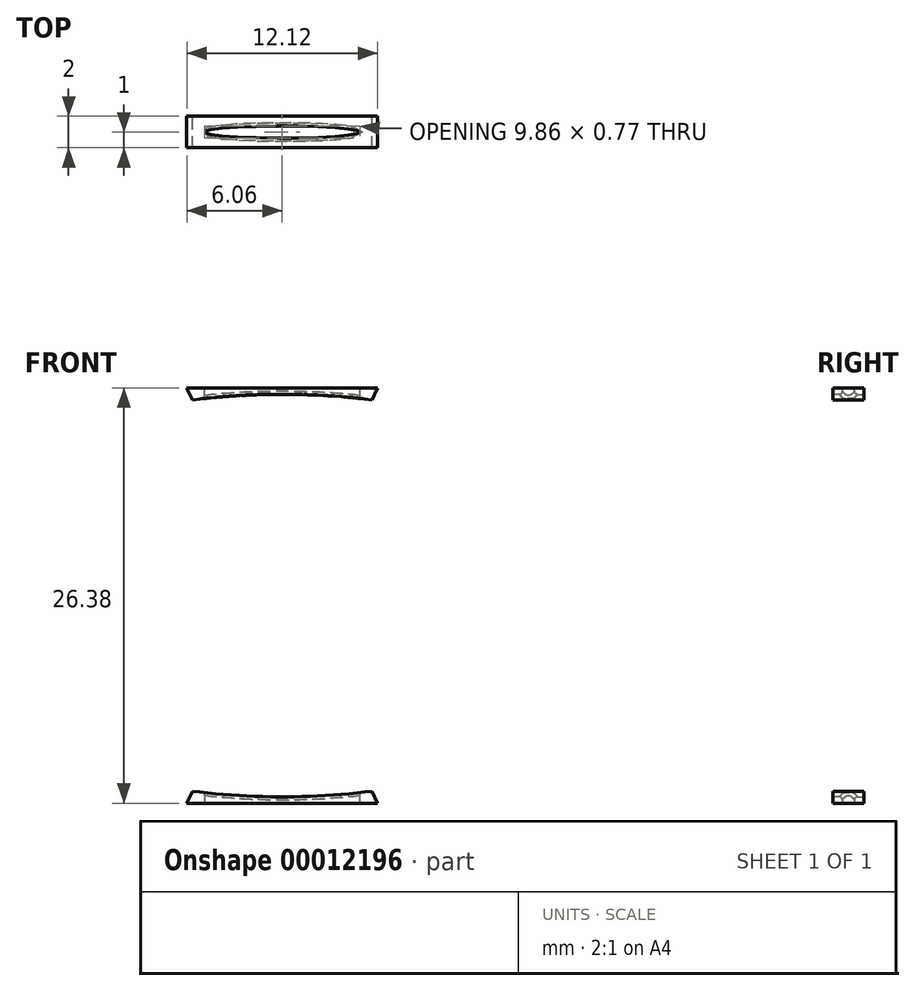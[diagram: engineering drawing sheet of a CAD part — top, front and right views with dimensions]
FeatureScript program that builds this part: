
annotation { "Feature Type Name" : "Feature", "Feature Type Description" : "" }
export const myFeature = defineFeature(function(context is Context, id is Id, definition is map)
    precondition{}
    {
        {
            var Q0;
            Q0=qCreatedBy(makeId("Front.planeOp"),FACE);
            var sketch = newSketch(context, id + "F0", { "sketchPlane" : qUnion([Q0])});
            skEllipse(sketch, "E0", {"center": v(0, 0) * mm, "majorRadius": 24.48 * mm, "minorRadius": 12.78 * mm, "majorAxis": v(1, 0)});
            skFitSpline(sketch, "E1.0", {"points": [v(25.2, -1.41) * mm, v(25.33, 0) * mm, v(25.2, 1.41) * mm, v(24.67, 3.25) * mm, v(23.65, 5) * mm, v(22.19, 6.6) * mm, v(20.44, 8.13) * mm, v(17.8, 9.8) * mm, v(14.6, 11.18) * mm, v(11.77, 12.06) * mm, v(8.8, 12.8) * mm, v(5.68, 13.29) * mm, v(2.45, 13.54) * mm, v(0, 13.6) * mm, v(-2.45, 13.54) * mm, v(-5.68, 13.29) * mm, v(-8.8, 12.8) * mm, v(-11.77, 12.06) * mm, v(-14.6, 11.18) * mm, v(-17.8, 9.8) * mm, v(-20.44, 8.13) * mm, v(-22.19, 6.6) * mm, v(-23.65, 5) * mm, v(-24.67, 3.25) * mm, v(-25.2, 1.41) * mm, v(-25.33, 0) * mm, v(-25.2, -1.41) * mm, v(-24.67, -3.25) * mm, v(-23.65, -5) * mm, v(-22.19, -6.6) * mm, v(-20.44, -8.13) * mm, v(-17.8, -9.8) * mm, v(-14.6, -11.18) * mm, v(-11.77, -12.06) * mm, v(-8.8, -12.8) * mm, v(-5.68, -13.29) * mm, v(-2.45, -13.54) * mm, v(0, -13.6) * mm, v(2.45, -13.54) * mm, v(5.68, -13.29) * mm, v(8.8, -12.8) * mm, v(11.77, -12.06) * mm, v(14.6, -11.18) * mm, v(17.8, -9.8) * mm, v(20.44, -8.13) * mm, v(22.19, -6.6) * mm, v(23.65, -5) * mm, v(24.67, -3.25) * mm, v(25.2, -1.41) * mm, v(25.33, 0) * mm, v(25.2, 1.41) * mm, v(25.2, -1.41) * mm]});
            skLineSegment(sketch, "E2", {"start": v(0, 0) * mm, "end": v(6.06, 13.19) * mm});
            skLineSegment(sketch, "E3", {"start": v(6.06, 13.19) * mm, "end": v(-6.06, 13.19) * mm});
            skLineSegment(sketch, "E4", {"start": v(-6.06, 13.19) * mm, "end": v(0, 0) * mm});
            skLineSegment(sketch, "E5", {"start": v(0, 0) * mm, "end": v(-6.06, -13.19) * mm});
            skLineSegment(sketch, "E6", {"start": v(0, 0) * mm, "end": v(6.06, -13.19) * mm});
            skLineSegment(sketch, "E7", {"start": v(6.06, -13.19) * mm, "end": v(-6.06, -13.19) * mm});
            skSolve(sketch);
        }
        {
            var Q0;
            {var subQ1=sQuery(id+"F0.wireOp",EDGE,"E0");var subQ8=sQuery(id+"F0.wireOp",EDGE,"E2");var subQ10=makeQuery(id+"F0.imprint","INTERSECT",VERTEX,{"derivedFrom":[subQ1,subQ8]});Q0=makeQuery(id+"F0.imprint","IMPRINT",FACE,{"disambiguationData":[TD([[makeQuery(id+"F0.imprint","IMPRINT",EDGE,{"disambiguationData":[TD([[subQ10,-1.0]])],"derivedFrom":subQ1}),-1.0]])]});}
            var Q1;
            {var subQ1=sQuery(id+"F0.wireOp",EDGE,"E0");var subQ5=sQuery(id+"F0.wireOp",EDGE,"E2");var subQ6=makeQuery(id+"F0.imprint","INTERSECT",VERTEX,{"derivedFrom":[subQ1,subQ5]});Q1=makeQuery(id+"F0.imprint","IMPRINT",FACE,{"disambiguationData":[TD([[makeQuery(id+"F0.imprint","IMPRINT",EDGE,{"disambiguationData":[TD([[subQ6,1.0]])],"derivedFrom":subQ1}),-1.0]])]});}
            var Q2;
            {var subQ1=sQuery(id+"F0.wireOp",EDGE,"E0");var subQ5=sQuery(id+"F0.wireOp",EDGE,"E4");var subQ6=makeQuery(id+"F0.imprint","INTERSECT",VERTEX,{"derivedFrom":[subQ1,subQ5]});Q2=makeQuery(id+"F0.imprint","IMPRINT",FACE,{"disambiguationData":[TD([[makeQuery(id+"F0.imprint","IMPRINT",EDGE,{"disambiguationData":[TD([[subQ6,-1.0]])],"derivedFrom":subQ1}),-1.0]])]});}
            var Q3;
            {var subQ5=sQuery(id+"F0.wireOp",EDGE,"E0");var subQ8=sQuery(id+"F0.wireOp",EDGE,"E5");var subQ9=makeQuery(id+"F0.imprint","INTERSECT",VERTEX,{"derivedFrom":[subQ5,subQ8]});Q3=makeQuery(id+"F0.imprint","IMPRINT",FACE,{"disambiguationData":[TD([[makeQuery(id+"F0.imprint","IMPRINT",EDGE,{"disambiguationData":[TD([[subQ9,-1.0]])],"derivedFrom":subQ5}),-1.0]])]});}
            extrude(context, id + "F1", {"entities" : qUnion([Q0, Q1, Q2, Q3]), "depth" : 1 * mm, "hasSecondDirection" : true, "secondDirectionOppositeDirection" : true, "secondDirectionDepth" : 1 * mm});
        }
        {
            var Q0;
            Q0=makeQuery(id+"F1.opExtrude","SWEPT_FACE",FACE,{"disambiguationData":[OSD([sQuery(id+"F0.wireOp",EDGE,"E3")])]});
            var sketch = newSketch(context, id + "F2", { "sketchPlane" : qUnion([Q0])});
            skLineSegment(sketch, "E8.bottom", {"start": v(-6.06, 1) * mm, "end": v(6.06, 1) * mm});
            skLineSegment(sketch, "E8.top", {"start": v(-6.06, -1) * mm, "end": v(6.06, -1) * mm});
            skLineSegment(sketch, "E8.left", {"start": v(-6.06, 1) * mm, "end": v(-6.06, -1) * mm});
            skLineSegment(sketch, "E8.right", {"start": v(6.06, 1) * mm, "end": v(6.06, -1) * mm});
            skLineSegment(sketch, "E9", {"start": v(0, 0.38) * mm, "end": v(0, 1) * mm});
            skEllipse(sketch, "E10", {"center": v(0, 0) * mm, "majorRadius": 4.93 * mm, "minorRadius": 0.38 * mm, "majorAxis": v(1, 0)});
            skSolve(sketch);
        }
        {
            var Q0;
            Q0=makeQuery(id+"F2.imprint","IMPRINT",FACE,{"disambiguationData":[TD([[makeQuery(id+"F2.imprint","IMPRINT",EDGE,{"derivedFrom":sQuery(id+"F2.wireOp",EDGE,"E10")}),1.0]])]});
            var Q1;
            Q1=sQuery(id+"F2.wireOp",EDGE,"E10");
            extrude(context, id + "F3", {"entities" : qUnion([Q0]), "operationType" : NewBodyOperationType.REMOVE, "surfaceEntities" : qUnion([Q1]), "endBound" : BoundingType.THROUGH_ALL, "oppositeDirection" : true, "depth" : 25 * mm});
        }
        {
            var Q0;
            Q0=makeQuery(id+"F3.boolean.opBoolean","COPY",EDGE,{"derivedFrom":makeQuery(id+"F3.opExtrude","CAP_EDGE",EDGE,{"disambiguationData":[OSD([sQuery(id+"F2.wireOp",EDGE,"E10")])],"isStart":true})});
            var Q1;
            Q1=makeQuery(id+"F3.boolean.opBoolean","INTERSECT",EDGE,{"disambiguationData":[OD(0.0)],"derivedFrom":[makeQuery(id+"F1.opExtrude","SWEPT_FACE",FACE,{"disambiguationData":[OSD([sQuery(id+"F0.wireOp",EDGE,"E0")])]}),makeQuery(id+"F3.opExtrude","SWEPT_FACE",FACE,{"disambiguationData":[OSD([sQuery(id+"F2.wireOp",EDGE,"E10")])]})]});
            var Q2;
            Q2=makeQuery(id+"F3.boolean.opBoolean","INTERSECT",EDGE,{"disambiguationData":[OD(1.0)],"derivedFrom":[makeQuery(id+"F1.opExtrude","SWEPT_FACE",FACE,{"disambiguationData":[OSD([sQuery(id+"F0.wireOp",EDGE,"E0")])]}),makeQuery(id+"F3.opExtrude","SWEPT_FACE",FACE,{"disambiguationData":[OSD([sQuery(id+"F2.wireOp",EDGE,"E10")])]})]});
            var Q3;
            Q3=makeQuery(id+"F3.boolean.opBoolean","INTERSECT",EDGE,{"derivedFrom":[makeQuery(id+"F1.opExtrude","SWEPT_FACE",FACE,{"disambiguationData":[OSD([sQuery(id+"F0.wireOp",EDGE,"E1.0")])]}),makeQuery(id+"F3.opExtrude","SWEPT_FACE",FACE,{"disambiguationData":[OSD([sQuery(id+"F2.wireOp",EDGE,"E10")])]})]});
            fillet(context, id + "F4", {"entities" : qUnion([Q0, Q1, Q2, Q3]), "radius" : .2 * mm, "tangentPropagation" : true, "allowEdgeOverflow" : false});
        }
    });
